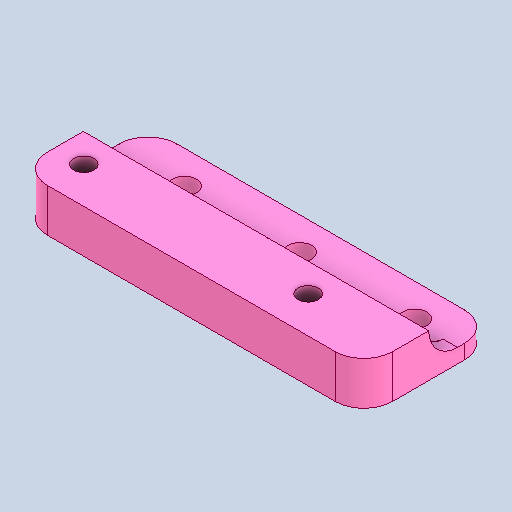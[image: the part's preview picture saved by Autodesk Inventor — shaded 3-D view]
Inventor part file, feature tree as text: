
AUTODESK INVENTOR PART (.ipt)
format: ipt  version: 2025.1 (Build 291241020, 241B)  size: 181,760 bytes
history: native  units: in
note: dims shown in document units (in); Inventor stores cm internally (conversion verified against a paired STEP export)
features: extrude x4, fillet x1, projected_geometry x1
ambient origin geometry x8: Origin, YZ Plane, XZ Plane, XY Plane, X Axis, Y Axis, Z Axis, Center Point
bodies: Solid1 (feature_tree)
feature tree (6):
  extrude  "Extrusion1"  Depth=0.125in
  extrude  "Extrusion2"  Depth=0.375in
  extrude  "Extrusion3"  Depth=1.125in
  fillet  "Fillet1"  Radius=3.0in
  extrude  "Extrusion4"  Depth=0.2087in
  projected_geometry  "Projected Loop1"
